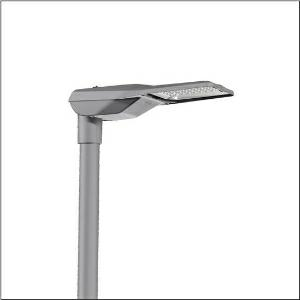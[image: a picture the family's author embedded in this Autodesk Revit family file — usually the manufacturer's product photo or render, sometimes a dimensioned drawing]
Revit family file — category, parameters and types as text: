
# Revit family: streetlight_sl_21_mini___st1_5a_5xe2p43s08gb_b57c
name_source: partatom
category: Lighting Fixtures
units: mm (PartAtom-declared; Revit-internal decimal feet)

## family parameters
Cut with Voids When Loaded = No
Host = Face
Light Source = No
Part Type = Normal
Room Calculation Point = No
Round Connector Dimension = Use Diameter
Shared = No

## types (1)
- --- (1 x LED, 6080 lm, 40.4 W, 4000K)
    Apparent Load = 40 VA
    CIE Flux Codes = 22 53 95 100 100
    Color Rendering = 70
    Color Temperature = 4000K
    Default Elevation = 1800 mm
    Description = Streetlight SL 21 mini, mast luminaire, primary light control with lens, of PMMA, primary optical cover: cover, of toughened safety glass, transparent, light distribution: ST1.5a, light emission: direct distribution, primary light characteristic: asymmetric, installation type: side-entry, post-top, LED, High Power LED, rated luminous flux: 6.080lm, luminous efficacy: 151lm/W, light colour: 740, colour temperature: 4000K, control gear: D4i, control: overheat protection, constant luminous flux control, time-dependent luminous flux control, flexible luminous flux parameterisation, pre-setting: logarithmic dimming characteristic, mains connection: 220..240V, AC, 50/60Hz, start of lifetime: 40W, end of service life: 41W, reduction: 19W, luminaire housing, of diecast aluminium, powder-coated, Siteco® metallic grey (DB 702S), corrosivity category C5 mid according to DIN EN ISO 12944, please order mast flange separately, inclination adjustable: 0°, 5°, 10°, 15°, sealing non-destructively replaceable, multi-level sealing system, length: 628mm, width: 235mm, height: 110mm, mast flange for spigot size: 42mm (side-entry): 5XC10008XM4, 60/48mm (side-entry/post-top): 5XC10108XM2, 76/60mm (side-entry/post-top): 5XC10108XM1, mounting height: 4..8m, Smart Interface above, protection rating (complete): IP66, insulation class (complete): insulation class II (safety insulation), certification: CE, ENEC, ENEC+, VDE, impact resistance: IK10, permissible operating ambient temperature for outdoor applications: -40..+50°C, standard-compliant lighting for roads and squares, packaging unit: 1 piece

Light Distribution: ST1.5a
    Height = 110 mm
    Lamp = 1 x LED
    Lamp Light Flux = 6080 lm
    Lamp Power = 40.4 W
    Lamp count = 1
    Length = 625 mm
    Luminous efficacy = 151 lm/W
    Manufacturer = Siteco
    ModVariant = No
    Model = 5XE2P43S08GB
    Number of Poles = 1
    OnlyDefault = Yes
    Power Factor = 1
    Product Name = Streetlight SL 21 mini | ST1.5a
    Product group = mast luminaire | pylon top
    ProductGroupID = 6100
    Protection Class = Protection class II
    Protection Degree = IP 66
    RLX_Detail_Level = 1
    RLX_Emergency_Light_Flux = 0 lm
    RLX_Emergency_Type = 0
    RLX_Emergency_Type_DB = No
    RlxData = <blob elided: 29745 chars, md5=c5296e92>
    Socket = socket
    Standby Power = 0 W
    System Light Flux = 6080 lm
    System Power = 40 W
    Type Comments = factory setting: luminous flux: 100 % | dim-lin: 254 | 812 mA
    Type Image = l_1003515.jpg
    URL = http://relux.com
    VarID = @adj_175676
    Voltage = 0 V
    Weight = 0.00 kg
    Width = 234 mm

## geometry (parser evidence)
native form markers: Blend x4, Sweep x10
no freeform markers — native parametric forms only
